# Revit family: IS_Joy_BD467_BIM_NL
name_source: partatom
category: Plumbing Fixtures
units: mm (PartAtom-declared; Revit-internal decimal feet)

## family parameters
Always vertical = No
Cut with Voids When Loaded = No
OmniClass Number = 23.45.55.17
OmniClass Title = Mixing Faucets
Part Type = Normal
Room Calculation Point = No
Round Connector Dimension = Use Diameter
Shared = No
Work Plane-Based = No

## types (4) — shared parameters
Accesoires = https://www.idealstandard.nl
Accessories = https://www.idealstandard.nl
Afmetingen = 48 x 159 x 188 mm
AfstandsEenheid = Millimeter
AssetType = Fixed
Auteur = Ideal Standard
BIMObjectName = ISI_IdealStandard_Washbasin manual water supply sets_Joy_BD467
BIMobject category = Taps & Mixers
BIMobject category code = sanitary-taps-mixers
BIMobject main category = Sanitary
BIMobject main category code = sanitary
Beschrijvinggarantie = Herstellergarantie
BimObjectNaam = ISI_IdealStandard_Washbasin manual water supply sets_Joy_BD467
Brand = Ideal Standard
Brand url = https://www.idealstandard.nl
ConnectionType = Fixed
CurrencyUnit = €
Date of publishing = 20/06/2023
Diepte = 48 mm
DistributedBy = Ideal Standard
DurationUnit = Years
Edition number = 1
ExpectedLife = 30
FaucetFunction = MIXED
FaucetOperation = OTHER
FaucetType = OTHER
Garantieonderdelen = 5
Garantieunits = Jaren
GemaaktOp = 20/06/2023
Help = https://www.idealstandard.nl
Hoogte = 188,067534590889
Hulp = https://www.idealstandard.nl
IFC Classification = Sanitary Terminal
IfcExportAs = IfcValveType
IfcExportType = FAUCET
Installatieinstructies = https://www.idealstandard.nl
Installation instructions = https://www.idealstandard.nl
InstallationInstructions = https://www.idealstandard.nl
IsBuiltIn = No
IsHighPressure = No
Lengte = 159 mm
LinearUnits = milimeter
MaintenanceInformation = https://www.idealstandard.nl
Manufacturer = Ideal Standard
Manufacturer name = Ideal Standard
ManufacturerURL = https://www.idealstandard.nl
Materiaal = Messing
Material = Brass
Material main = Brass
Merk = Ideal Standard
ModelNumber = BD467
NBS Reference Code = 35-79-95
NBS Reference Description = Wash Basin And Trough Water Supply Fittings
Name = Washbasin manual water supply sets_Joy_BD467_IdealStandard
NettWeight = 1,554
Nettogewicht = 1.554
NominalHeight = 188 mm
NominalLength = 159 mm
NominalWidth = 48 mm
OmniClass Code = 23-31 11 00
OmniClass Description = Faucets
OppervlakteEenheid = Millimeter
Product Guid = 22625a02-7386-45d4-86e7-4acdba8151ca
Product SKU = BD467
Product certification = https://www.idealstandard.nl
Product data url = https://bimobject.com
Product family = JOY
Product group = Taps & Mixers
Product name = Joy Basin Mixer with Long Handle, metal PUW
Product url = https://www.idealstandard.nl
ProductInformation = https://www.idealstandard.nl
ProductSoort = Sanitair
Productinformatie = https://www.idealstandard.nl
QR code = http://bimobject.com
Revisie = 1
Shape = Sculptured
Size = 48 x 159 x 188 mm
Space = Internal
SpareParts = https://www.idealstandard.nl
SustainabilityPerformance = https://www.idealstandard.nl
Technical description = https://www.idealstandard.nl
Telefoonnummer = 077 355 08 08
TestPressure = 10 Bar
Typeconnectie = Installation
UNSPSC Code = 301815
URL = https://www.idealstandard.nl
Uniclass 1.4 Code = L725111
Uniclass 1.4 Description = Mixer taps
Uniclass 2.0 Code = PR-35-79-95
Uniclass 2.0 Description = Wash Basin And Trough Water Supply Fittings
Uniclass 2015 Code = Pr_40_20_87_98
Uniclass 2015 Name = Washbasin taps
Uniclass2015Beschrijving = Pr_40_20_87_98
Uniclass2015Code = Pr_40_20_87_98
Uniclass2015Referentie = Pr_40_20_87_98
Uniclass2015Title = Washbasin taps
Uniclass2015Version = v1.1
Urlproducent = https://www.idealstandard.nl
ValutaEenheid = €
Versie = 1
Version = 1
VolumeUnits = Litres
Volumeunits = Liters
Vorm = zylindrisch
WRASURL = https://www.wras.co.uk
WarrantyDescription = Manufacturers Warranty
WarrantyDurationParts = 5
WarrantyDurationUnit = year
WarrantyGuarantorParts = https://www.idealstandard.nl
Wisselstukken = https://www.idealstandard.nl
WorkingPressure = 3bar
Youtube clip = https://www.youtube.com
zero-valued in all types: Breedte, BrutoGewicht, Cost, Default Elevation, Vervangingskosten

## per-type parameters (varying)
| type | Afwerking | Artikelnummer | Artikelomschrijving | Artikelreferentie | BarCode | Barcode | Color | Description | Features | Finish | GTIN code | Kleur | MainColor | Model | ModelReference |
| BD467A2 - Joy Basin Mixer with Long Handle, metal PUW - Brushed Gold | Geborsteld Goud | BD467A2 | Joy Wastafelmengkraan met Lange Hendel, metalen PUW - Geborsteld Goud | Joy Wastafelmengkraan met Lange Hendel, metalen PUW - Geborsteld Goud | 3800861111122 | 3800861111122 | Brushed Gold | Joy Basin Mixer with Long Handle, metal PUW - Brushed Gold | Basin Mixer with Long Handle, metal PUW - Brushed Gold | Brushed Gold | 3800861111122 | Geborsteld Goud | Brushed Gold | BD467A2 | BD467A2 |
| BD467A5 - Joy Basin Mixer with Long Handle, metal PUW - Magnetic Grey | Magnetisch grijs | BD467A5 | Joy Wastafelmengkraan met Lange Hendel, metalen PUW - Magnetisch Grijs | Joy Wastafelmengkraan met Lange Hendel, metalen PUW - Magnetisch Grijs | 3800861111146 | 3800861111146 | Magnetic grey | Joy Basin Mixer with Long Handle, metal PUW - Magnetic Grey | Basin Mixer with Long Handle, metal PUW - Magnetic Grey | Magnetic grey | 3800861111146 | Magnetisch grijs | Magnetic grey | BD467A5 | BD467A5 |
| BD467AA - Joy Basin Mixer with Long Handle, metal PUW - Chrome | Chroom | BD467AA | Joy Wastafelmengkraan met Lange Hendel, metalen PUW - Chroom | Joy Wastafelmengkraan met Lange Hendel, metalen PUW - Chroom | 3800861111108 | 3800861111108 | Chrome | Joy Basin Mixer with Long Handle, metal PUW - Chrome | Basin Mixer with Long Handle, metal PUW - Chrome | Chrome | 3800861111108 | Chroom | Chrome | BD467AA | BD467AA |
| BD467GN - Joy Basin Mixer with Long Handle, metal PUW - Silver Storm | Zilveren storm | BD467GN | Joy Wastafelmengkraan met Lange Hendel, metalen PUW - Zilveren Storm | Joy Wastafelmengkraan met Lange Hendel, metalen PUW - Zilveren Storm | 3800861111160 | 3800861111160 | Silver storm | Joy Basin Mixer with Long Handle, metal PUW - Silver Storm | Basin Mixer with Long Handle, metal PUW - Silver Storm | Silver storm | 3800861111160 | Zilveren storm | Silver storm | BD467GN | BD467GN |

note: column(s) folded — value = type name in every type: Eigenschappen, Referentie

## geometry (parser evidence)
native form markers: Blend x2, Sweep x3
no freeform markers — native parametric forms only
